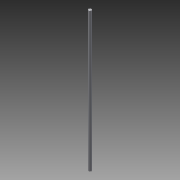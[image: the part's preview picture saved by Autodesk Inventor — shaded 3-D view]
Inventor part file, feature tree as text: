
AUTODESK INVENTOR PART (.ipt)
format: ipt  version: 2013 (Build 170138000, 138)  size: 69,632 bytes
history: native  units: in
note: dims shown in document units (in); Inventor stores cm internally (conversion verified against a paired STEP export)
features: extrude x1, sketch x1
ambient origin geometry x8: Origin, YZ Plane, XZ Plane, XY Plane, X Axis, Y Axis, Z Axis, Center Point
bodies: Solid1 (feature_tree)
feature tree (2):
  extrude  "Extrusion1"  Depth=19.0in TaperAngle=0.0deg
  sketch  "Sketch1"  dims[d0=0.375in d1=19.0in d2=0.0in]
